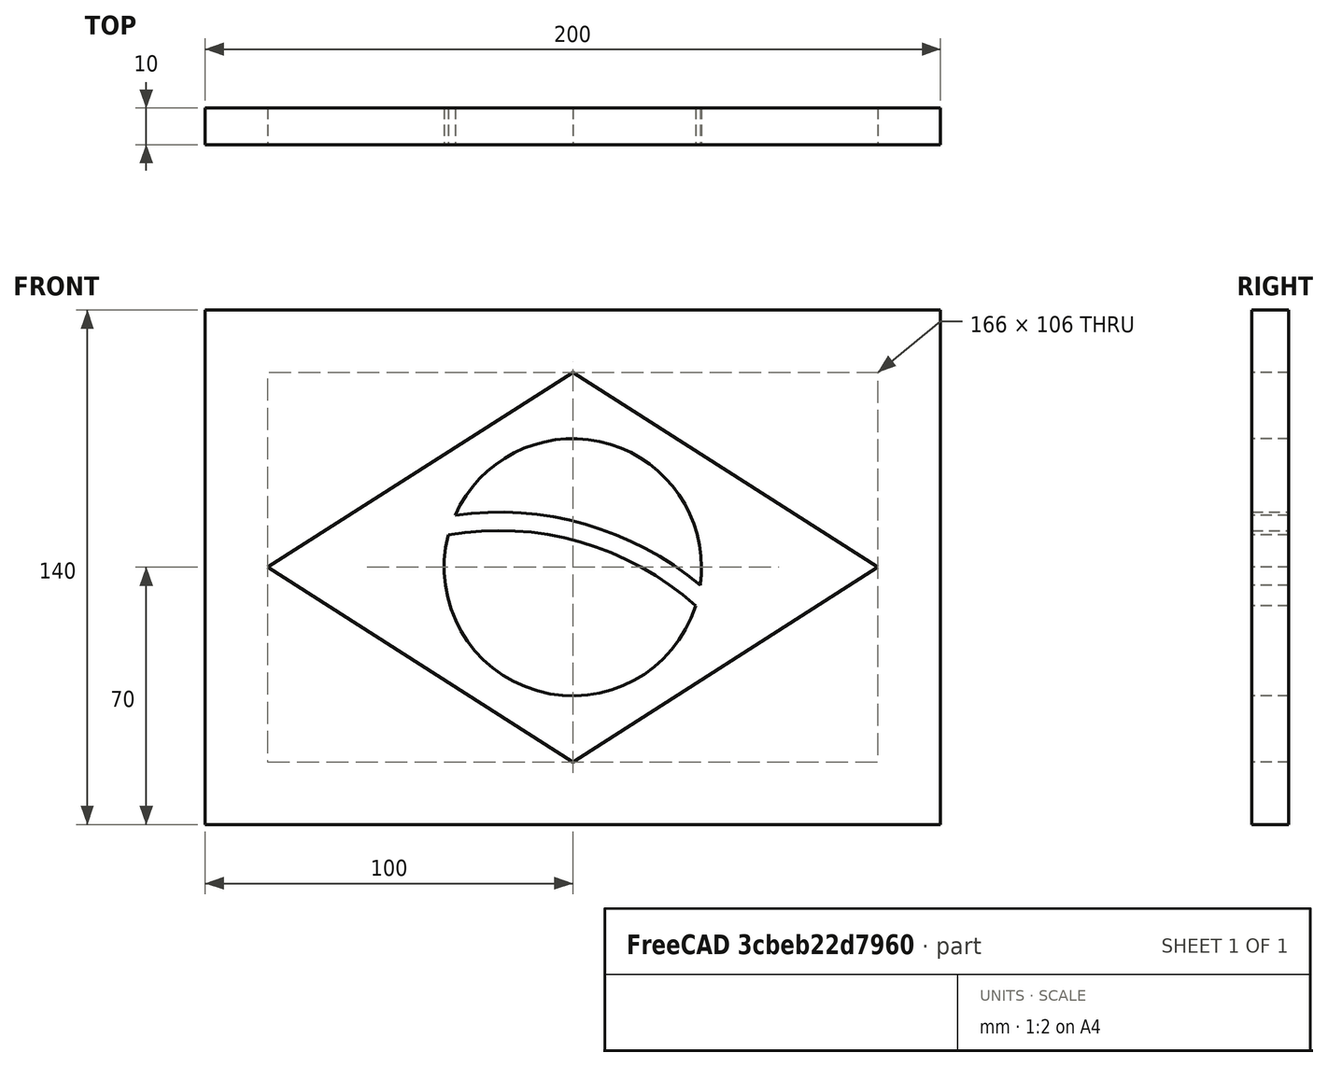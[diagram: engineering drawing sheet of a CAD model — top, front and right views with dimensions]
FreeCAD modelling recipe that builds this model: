
FCSTD DOCUMENT  (FreeCAD 0.17R13247 (Git))
Label: BANDEIRA BRASIL
License: All rights reserved
LicenseURL: http://en.wikipedia.org/wiki/All_rights_reserved
objects: Part::FeaturePython×4, Part::Cut×3
note: 7 computed .brp shape members not serialized (recipe doc carries the construction recipe); baked Part::Feature solids carry a one-line shape summary decoded from their .brp

FEATURE [Part::FeaturePython] BANDEIRA_1_01  # a2plus imported part (geometry in sourceFile) (typed FeaturePython)
  Placement = pos=(0,0,0) rot=(1,0,0;1.5708rad)
  fixedPosition = true
  sourceFile = <path>
  timeLastImport = 1.5227e+09
  updateColors = true
FEATURE [Part::FeaturePython] BANDEIRA_2_01  # a2plus imported part (geometry in sourceFile) (typed FeaturePython)
  Placement = pos=(0,0,0) rot=(1,0,0;1.5708rad)
  fixedPosition = false
  sourceFile = <path>
  timeLastImport = 1.5227e+09
  updateColors = true
FEATURE [Part::Cut] Cut
  Base = -> BANDEIRA_2_01
  Tool = -> BANDEIRA_1_01
FEATURE [Part::FeaturePython] BANDEIRA_3_01  # a2plus imported part (geometry in sourceFile) (typed FeaturePython)
  Placement = pos=(0,0,0) rot=(1,0,0;1.5708rad)
  fixedPosition = false
  sourceFile = <path>
  timeLastImport = 1.5227e+09
  updateColors = true
FEATURE [Part::Cut] Cut001
  Base = -> BANDEIRA_3_01
  Tool = -> Cut
FEATURE [Part::FeaturePython] BANDEIRA_4_01  # a2plus imported part (geometry in sourceFile) (typed FeaturePython)
  Placement = pos=(0,0,0) rot=(1,0,0;1.5708rad)
  fixedPosition = false
  sourceFile = <path>
  timeLastImport = 1.5227e+09
  updateColors = true
FEATURE [Part::Cut] Cut002
  Base = -> BANDEIRA_4_01
  Tool = -> Cut001
note: 4 file-system paths scrubbed to <path> (originals preserved in the JSON sidecar)
